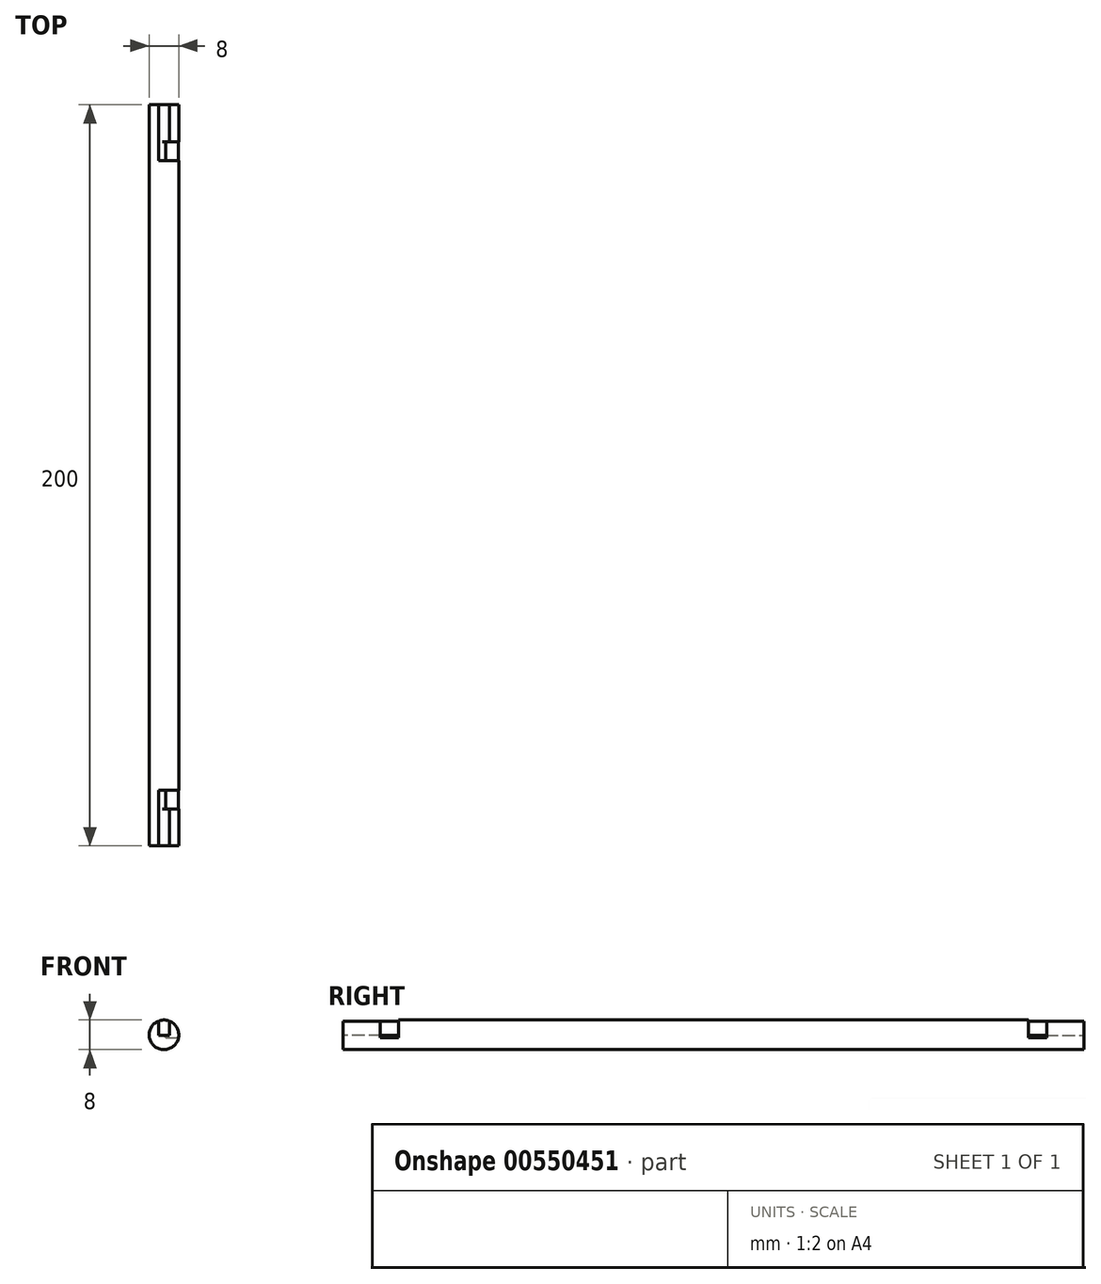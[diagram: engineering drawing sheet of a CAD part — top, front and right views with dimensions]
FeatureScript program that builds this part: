
annotation { "Feature Type Name" : "Feature", "Feature Type Description" : "" }
export const myFeature = defineFeature(function(context is Context, id is Id, definition is map)
    precondition{}
    {
        {
            var Q0;
            Q0=qCreatedBy(makeId("Front.planeOp"),FACE);
            var sketch = newSketch(context, id + "F0", { "sketchPlane" : qUnion([Q0])});
            skCircle(sketch, "E0", {"center": v(-39.58, 19.26) * mm, "radius": 4 * mm});
            skLineSegment(sketch, "E1", {"start": v(-39.58, 19.26) * mm, "end": v(-39.58, 15.26) * mm});
            skLineSegment(sketch, "E2", {"start": v(-39.58, 15.26) * mm, "end": v(-39.58, 12.94) * mm});
            skSolve(sketch);
        }
        {
            var Q0;
            Q0=makeQuery(id+"F0.imprint","IMPRINT",FACE,{"disambiguationData":[TD([[makeQuery(id+"F0.imprint","IMPRINT",EDGE,{"derivedFrom":sQuery(id+"F0.wireOp",EDGE,"E0")}),1.0]])]});
            extrude(context, id + "F1", {"entities" : qUnion([Q0]), "depth" : 200 * mm, "offsetDistance" : 25 * mm});
        }
        {
            var Q0;
            Q0=makeQuery(id+"F1.opExtrude","CAP_FACE",FACE,{"disambiguationData":[OSD([sQuery(id+"F0.wireOp",EDGE,"E0")])],"isStart":true});
            var sketch = newSketch(context, id + "F2", { "sketchPlane" : qUnion([Q0])});
            skLineSegment(sketch, "E3", {"start": v(41.08, 23.26) * mm, "end": v(41.08, 19.06) * mm});
            skLineSegment(sketch, "E4", {"start": v(41.08, 19.06) * mm, "end": v(38.08, 19.06) * mm});
            skLineSegment(sketch, "E5", {"start": v(38.08, 19.06) * mm, "end": v(38.08, 23.26) * mm});
            skLineSegment(sketch, "E6", {"start": v(41.08, 23.26) * mm, "end": v(38.08, 23.26) * mm});
            skSolve(sketch);
        }
        {
            var Q0;
            {var subQ5=sQuery(id+"F2.wireOp",EDGE,"E4");Q0=makeQuery(id+"F2.imprint","IMPRINT",FACE,{"disambiguationData":[TD([[makeQuery(id+"F2.imprint","IMPRINT",EDGE,{"derivedFrom":subQ5}),-1.0]])]});}
            extrude(context, id + "F3", {"entities" : qUnion([Q0]), "operationType" : NewBodyOperationType.REMOVE, "oppositeDirection" : true, "depth" : 15 * mm, "offsetDistance" : 25 * mm});
        }
        {
            var Q0;
            Q0=makeQuery(id+"F1.opExtrude","CAP_FACE",FACE,{"disambiguationData":[OSD([sQuery(id+"F0.wireOp",EDGE,"E0")])],"isStart":false});
            var sketch = newSketch(context, id + "F4", { "sketchPlane" : qUnion([Q0])});
            skLineSegment(sketch, "E7", {"start": v(-38.05, 23.27) * mm, "end": v(-38.05, 19.07) * mm});
            skLineSegment(sketch, "E8", {"start": v(-38.05, 19.07) * mm, "end": v(-41.05, 19.07) * mm});
            skLineSegment(sketch, "E9", {"start": v(-41.05, 19.07) * mm, "end": v(-41.05, 23.27) * mm});
            skLineSegment(sketch, "E10", {"start": v(-38.05, 23.27) * mm, "end": v(-41.05, 23.27) * mm});
            skSolve(sketch);
        }
        {
            var Q0;
            {var subQ0=sQuery(id+"F4.wireOp",EDGE,"E8");Q0=makeQuery(id+"F4.imprint","IMPRINT",FACE,{"disambiguationData":[TD([[makeQuery(id+"F4.imprint","IMPRINT",EDGE,{"derivedFrom":subQ0}),-1.0]])]});}
            extrude(context, id + "F5", {"entities" : qUnion([Q0]), "operationType" : NewBodyOperationType.REMOVE, "oppositeDirection" : true, "depth" : 15 * mm, "offsetDistance" : 25 * mm});
        }
        {
            var Q0;
            Q0=qCreatedBy(makeId("Right.planeOp"),FACE);
            cPlane(context, id + "F6", {"entities" : qUnion([Q0]), "cplaneType" : CPlaneType.OFFSET, "offset" : 35.58 * mm, "oppositeDirection" : true, "width" : 150 * mm, "height" : 150 * mm});
        }
        {
            var Q0;
            Q0=qCreatedBy(id+"F6.planeOp",FACE);
            var sketch = newSketch(context, id + "F7", { "sketchPlane" : qUnion([Q0])});
            skLineSegment(sketch, "E11", {"start": v(-10, 22.97) * mm, "end": v(-15, 22.98) * mm});
            skLineSegment(sketch, "E12", {"start": v(-10, 22.97) * mm, "end": v(-10, 18.47) * mm});
            skLineSegment(sketch, "E13", {"start": v(-15, 22.98) * mm, "end": v(-15, 18.47) * mm});
            skLineSegment(sketch, "E14", {"start": v(-15, 18.47) * mm, "end": v(-10, 18.47) * mm});
            skLineSegment(sketch, "E15.MirrorCS", {"start": v(-190, 22.97) * mm, "end": v(-185, 22.98) * mm});
            skLineSegment(sketch, "E16.MirrorCS", {"start": v(-190, 22.97) * mm, "end": v(-190, 18.47) * mm});
            skLineSegment(sketch, "E17.MirrorCS", {"start": v(-185, 18.47) * mm, "end": v(-190, 18.47) * mm});
            skLineSegment(sketch, "E18.MirrorCS", {"start": v(-185, 22.98) * mm, "end": v(-185, 18.47) * mm});
            skSolve(sketch);
        }
        {
            var Q0;
            Q0=makeQuery(id+"F7.imprint","IMPRINT",FACE,{"disambiguationData":[TD([[makeQuery(id+"F7.imprint","IMPRINT",EDGE,{"derivedFrom":sQuery(id+"F7.wireOp",EDGE,"E15.MirrorCS")}),-1.0]])]});
            var Q1;
            Q1 = qSketchRegion(id + "F7", true);
            extrude(context, id + "F8", {"entities" : qUnion([Q0, Q1]), "operationType" : NewBodyOperationType.REMOVE, "oppositeDirection" : true, "depth" : 3.5 * mm, "offsetDistance" : 25 * mm});
        }
        {
            var Q0;
            Q0=makeQuery(id+"F8.boolean.opBoolean","INTERSECT",EDGE,{"derivedFrom":[makeQuery(id+"F3.boolean.opBoolean","COPY",FACE,{"derivedFrom":makeQuery(id+"F3.opExtrude","SWEPT_FACE",FACE,{"disambiguationData":[OSD([sQuery(id+"F2.wireOp",EDGE,"E4")])]})}),makeQuery(id+"F8.opExtrude","CAP_FACE",FACE,{"disambiguationData":[OSD([sQuery(id+"F7.wireOp",EDGE,"E11"),sQuery(id+"F7.wireOp",EDGE,"E12"),sQuery(id+"F7.wireOp",EDGE,"E13"),sQuery(id+"F7.wireOp",EDGE,"E14")])],"isStart":false})]});
            var Q1;
            Q1=makeQuery(id+"F8.boolean.opBoolean","INTERSECT",EDGE,{"derivedFrom":[makeQuery(id+"F5.boolean.opBoolean","COPY",FACE,{"derivedFrom":makeQuery(id+"F5.opExtrude","SWEPT_FACE",FACE,{"disambiguationData":[OSD([sQuery(id+"F4.wireOp",EDGE,"E8")])]})}),makeQuery(id+"F8.opExtrude","CAP_FACE",FACE,{"disambiguationData":[OSD([sQuery(id+"F7.wireOp",EDGE,"E15.MirrorCS"),sQuery(id+"F7.wireOp",EDGE,"E16.MirrorCS"),sQuery(id+"F7.wireOp",EDGE,"E17.MirrorCS"),sQuery(id+"F7.wireOp",EDGE,"E18.MirrorCS")])],"isStart":false})]});
            fillet(context, id + "F9", {"entities" : qUnion([Q0, Q1]), "radius" : 1 * mm, "tangentPropagation" : true, "allowEdgeOverflow" : false});
        }
    });
